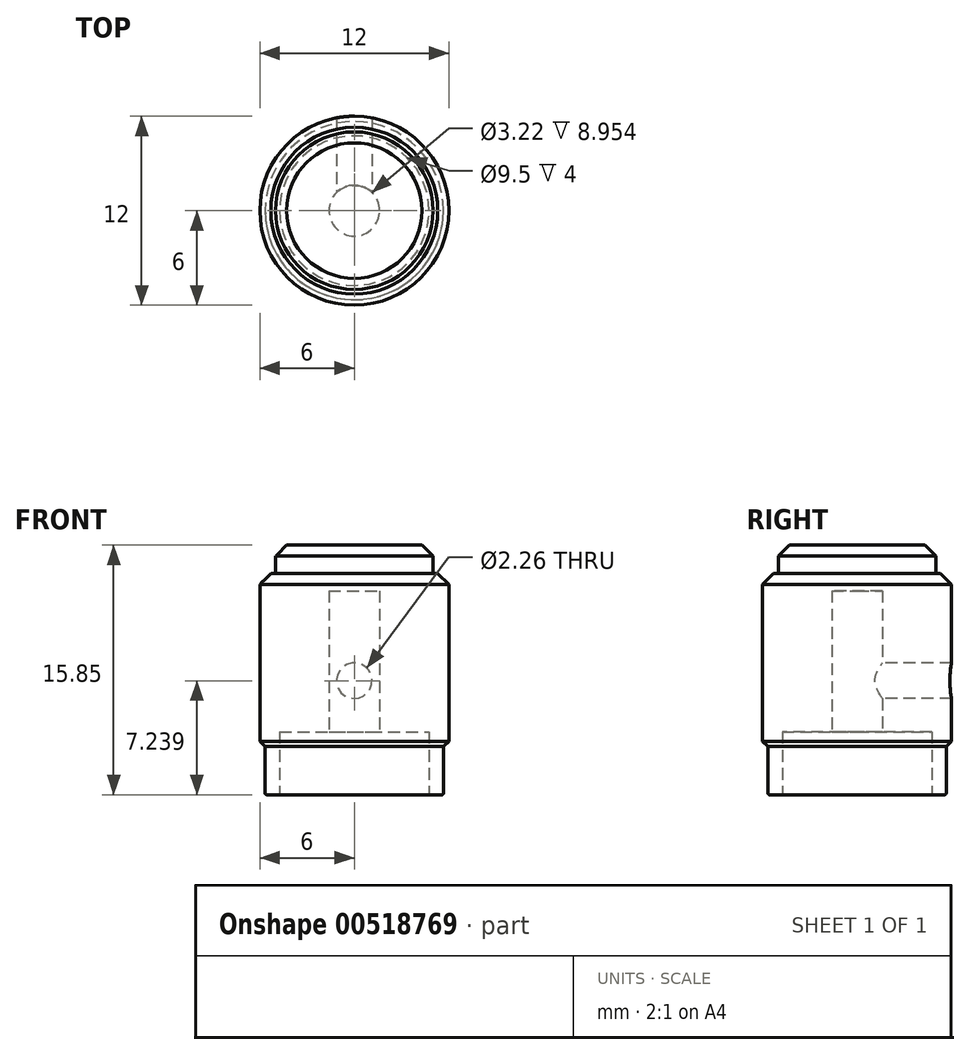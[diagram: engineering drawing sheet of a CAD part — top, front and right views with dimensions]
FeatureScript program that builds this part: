
annotation { "Feature Type Name" : "Feature", "Feature Type Description" : "" }
export const myFeature = defineFeature(function(context is Context, id is Id, definition is map)
    precondition{}
    {
        {
            var Q0;
            Q0=qCreatedBy(makeId("Front.planeOp"),FACE);
            var sketch = newSketch(context, id + "F0", { "sketchPlane" : qUnion([Q0])});
            skLineSegment(sketch, "E0.bottom", {"start": v(4.75, 0) * mm, "end": v(5.66, 0) * mm});
            skLineSegment(sketch, "E0.top", {"start": v(0, 15.85) * mm, "end": v(5, 15.85) * mm});
            skLineSegment(sketch, "E0.left", {"start": v(0, 4) * mm, "end": v(0, 15.85) * mm, "construction": true});
            skLineSegment(sketch, "E0.right", {"start": v(6, 2.7) * mm, "end": v(6, 14.05) * mm});
            skLineSegment(sketch, "E1", {"start": v(1.6, 4) * mm, "end": v(4.75, 4) * mm});
            skLineSegment(sketch, "E2", {"start": v(4.75, 4) * mm, "end": v(4.75, 0) * mm});
            skLineSegment(sketch, "E3", {"start": v(5.66, 0) * mm, "end": v(5.66, 2.7) * mm});
            skLineSegment(sketch, "E4", {"start": v(5.66, 2.7) * mm, "end": v(6, 2.7) * mm});
            skLineSegment(sketch, "E5", {"start": v(5, 15.85) * mm, "end": v(5, 14.05) * mm});
            skLineSegment(sketch, "E6", {"start": v(5, 14.05) * mm, "end": v(6, 14.05) * mm});
            skLineSegment(sketch, "E7", {"start": v(1.6, 4) * mm, "end": v(1.6, 12.95) * mm});
            skLineSegment(sketch, "E8", {"start": v(1.6, 12.95) * mm, "end": v(0, 12.95) * mm});
            skLineSegment(sketch, "E9", {"start": v(0, 15.85) * mm, "end": v(0, 12.95) * mm});
            skPoint(sketch, "E10", {"position": v(0, 7.24) * mm});
            skSolve(sketch);
        }
        {
            var Q0;
            Q0=qSketchRegion(id+"F0",true);
            var Q1;
            Q1=sQuery(id+"F0.wireOp",EDGE,"E0.left");
            revolve(context, id + "F1", {"entities" : qUnion([Q0]), "axis" : qUnion([Q1]), "revolveType" : RevolveType.FULL});
        }
        {
            var Q0;
            Q0=makeQuery(id+"F1.opRevolve","SWEPT_EDGE",EDGE,{"disambiguationData":[OSD([sQuery(id+"F0.wireOp",EDGE,"E0.right"),sQuery(id+"F0.wireOp",EDGE,"E6")])]});
            var Q1;
            Q1=makeQuery(id+"F1.opRevolve","SWEPT_EDGE",EDGE,{"disambiguationData":[OSD([sQuery(id+"F0.wireOp",EDGE,"E0.right"),sQuery(id+"F0.wireOp",EDGE,"E4")])]});
            var Q2;
            Q2=makeQuery(id+"F1.opRevolve","SWEPT_EDGE",EDGE,{"disambiguationData":[OSD([sQuery(id+"F0.wireOp",EDGE,"E0.top"),sQuery(id+"F0.wireOp",EDGE,"E5")])]});
            chamfer(context, id + "F2", {"entities" : qUnion([Q0, Q1, Q2]), "width" : 0.7 * mm, "tangentPropagation" : true});
        }
        {
            var Q0;
            Q0=makeQuery(id+"F1.opRevolve","SWEPT_EDGE",EDGE,{"disambiguationData":[OSD([sQuery(id+"F0.wireOp",EDGE,"E0.bottom"),sQuery(id+"F0.wireOp",EDGE,"E3")])]});
            fillet(context, id + "F3", {"entities" : qUnion([Q0]), "radius" : .1 * mm, "tangentPropagation" : true, "allowEdgeOverflow" : false});
        }
        {
            var Q0;
            Q0=sQuery(id+"F0.wireOp",VERTEX,"E10");
            var Q1;
            Q1=makeQuery(id+"F1.opRevolve","SWEPT_BODY",BODY,{"disambiguationData":[OSD([sQuery(id+"F0.wireOp",EDGE,"E0.bottom"),sQuery(id+"F0.wireOp",EDGE,"E0.top"),sQuery(id+"F0.wireOp",EDGE,"E0.right"),sQuery(id+"F0.wireOp",EDGE,"E1"),sQuery(id+"F0.wireOp",EDGE,"E2"),sQuery(id+"F0.wireOp",EDGE,"E3"),sQuery(id+"F0.wireOp",EDGE,"E4"),sQuery(id+"F0.wireOp",EDGE,"E5"),sQuery(id+"F0.wireOp",EDGE,"E6"),sQuery(id+"F0.wireOp",EDGE,"E7"),sQuery(id+"F0.wireOp",EDGE,"E8"),sQuery(id+"F0.wireOp",EDGE,"E9")])]});
            hole(context, id + "F4", {"style" : HoleStyle.SIMPLE, "endStyle" : HoleEndStyle.THROUGH, "standardTappedOrClearance" : lookupTablePath({ "standard" : "ANSI", "engagement" : "75%", "pitch" : "40 tpi", "size" : "#4", "type" : "Tapped" }), "standardBlindInLast" : lookupTablePath({ "standard" : "ANSI", "engagement" : "75%", "pitch" : "40 tpi", "size" : "#4", "type" : "Tapped" }), "holeDiameter" : 2.26 * mm, "showTappedDepth" : true, "isTappedThrough" : true, "tappedDepth" : 12 * mm, "tapClearance" : 3, "locations" : qUnion([Q0]), "scope" : qUnion([Q1]), "majorDiameter" : 2.84 * mm});
        }
    });
